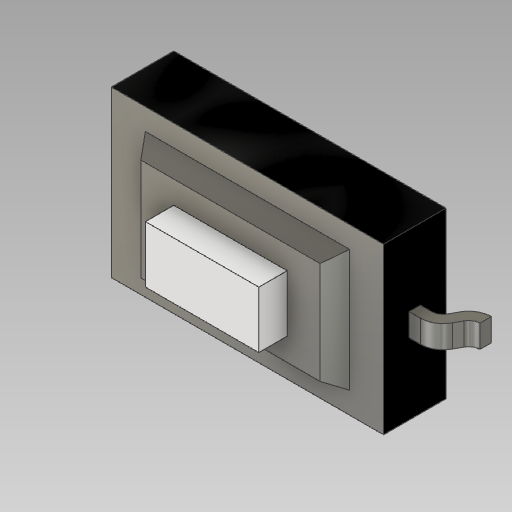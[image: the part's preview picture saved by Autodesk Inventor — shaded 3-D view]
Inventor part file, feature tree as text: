
AUTODESK INVENTOR PART (.ipt)
format: ipt  version: 2020 (Build 240168000, 168)  size: 197,120 bytes
history: native  units: in
note: dims shown in document units (in); Inventor stores cm internally (conversion verified against a paired STEP export)
features: sketch x6, extrude x2, plane x1, loft x1, sweep x1, mirror x1
ambient origin geometry x8: Origin, YZ Plane, XZ Plane, XY Plane, X Axis, Y Axis, Z Axis, Center Point
bodies: Solid1 (feature_tree)
feature tree (12):
  extrude  "Extrusion1"  Depth=0.1455in
  sketch  "Sketch2"  dims[d2=0.055in d3=0.0in d4=0.18in]
  plane  "Work Plane1"
  loft  "Loft1"
  extrude  "Extrusion2"  Depth=0.015in
  sweep  "Sweep1"
  mirror  "Mirror1"
  sketch  "Sketch1"  dims[d0=0.24in d1=0.1455in]
  sketch  "Sketch3"  dims[d5=0.1075in d6=0.015in]
  sketch  "Sketch4"  dims[d7=0.158in d8=0.09in]
  sketch  "Sketch5"  dims[d9=0.0in d10=90.0deg]
  sketch  "Sketch6"  dims[d11=0.0in d12=90.0deg d13=0.1in d14=0.05in d15=0.025in d16=0.0in d17=0.04in d18=0.005in d19=0.01in d20=0.015in d21=0.01in d22=0.02in d23=0.0in d24=0.0in]
